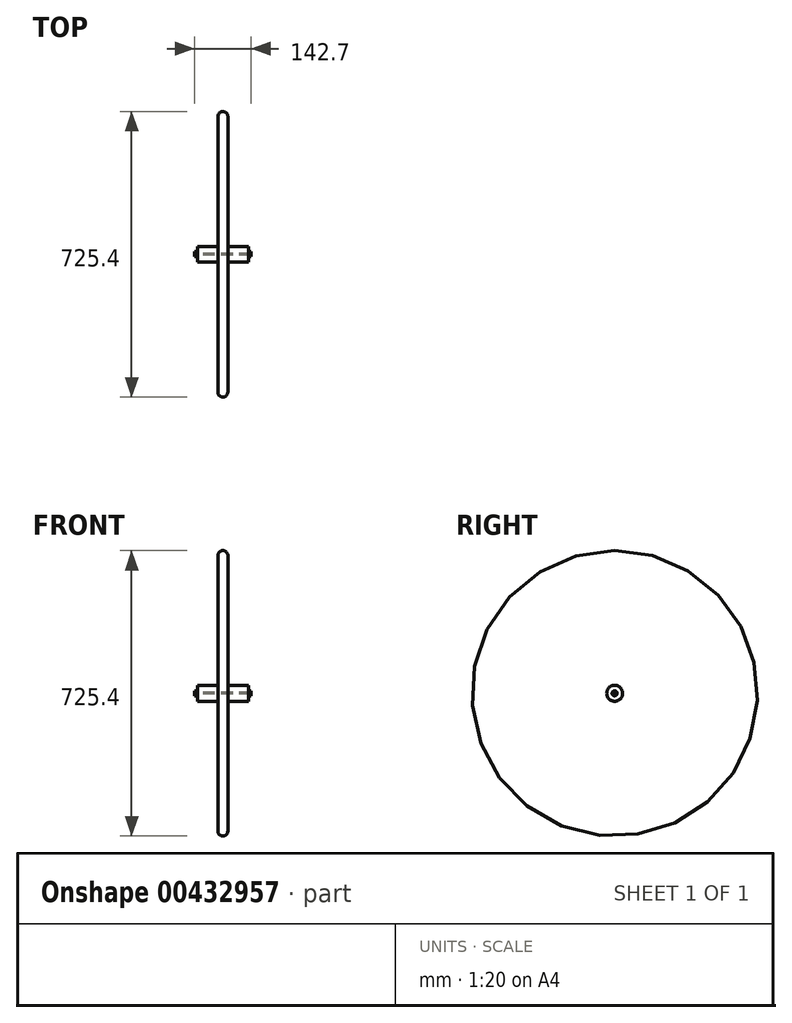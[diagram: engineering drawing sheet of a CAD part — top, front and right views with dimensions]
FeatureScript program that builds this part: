
annotation { "Feature Type Name" : "Feature", "Feature Type Description" : "" }
export const myFeature = defineFeature(function(context is Context, id is Id, definition is map)
    precondition{}
    {
        {
            var Q0;
            Q0=qCreatedBy(makeId("Top.planeOp"),FACE);
            var sketch = newSketch(context, id + "F0", { "sketchPlane" : qUnion([Q0])});
            skLineSegment(sketch, "E0", {"start": v(-65, 20.22) * mm, "end": v(-12.7, 20.22) * mm});
            skLineSegment(sketch, "E1", {"start": v(-75.47, 0) * mm, "end": v(74.77, 0) * mm});
            skLineSegment(sketch, "E2", {"start": v(65, 20.22) * mm, "end": v(65, 6.35) * mm});
            skLineSegment(sketch, "E3", {"start": v(65, 6.35) * mm, "end": v(65, 6.35) * mm});
            skLineSegment(sketch, "E4", {"start": v(71.35, 6.35) * mm, "end": v(65, 6.35) * mm});
            skLineSegment(sketch, "E5", {"start": v(-65, 20.22) * mm, "end": v(-65, 6.35) * mm});
            skLineSegment(sketch, "E6", {"start": v(-65, 6.35) * mm, "end": v(-71.35, 6.35) * mm});
            skLineSegment(sketch, "E7", {"start": v(-71.35, 6.35) * mm, "end": v(-71.35, 1.84) * mm});
            skLineSegment(sketch, "E8", {"start": v(71.35, 6.35) * mm, "end": v(71.35, 1.57) * mm});
            skLineSegment(sketch, "E9", {"start": v(-71.35, 1.84) * mm, "end": v(71.35, 1.57) * mm});
            skArc(sketch, "E10", {"start": v(12.7, 350) * mm, "mid": v(0, 362.7) * mm, "end": v(-12.7, 350) * mm});
            skLineSegment(sketch, "E11", {"start": v(12.7, 350) * mm, "end": v(12.7, 20.22) * mm});
            skLineSegment(sketch, "E12", {"start": v(-12.7, 350) * mm, "end": v(-12.7, 20.22) * mm});
            skLineSegment(sketch, "E13.trimOffspring", {"start": v(12.7, 20.22) * mm, "end": v(65, 20.22) * mm});
            skSolve(sketch);
        }
        {
            var Q0;
            Q0=makeQuery(id+"F0.imprint","IMPRINT",FACE,{"disambiguationData":[TD([[makeQuery(id+"F0.imprint","IMPRINT",EDGE,{"derivedFrom":sQuery(id+"F0.wireOp",EDGE,"E0")}),-1.0]])]});
            var Q1;
            Q1=sQuery(id+"F0.wireOp",EDGE,"E1");
            revolve(context, id + "F1", {"entities" : qUnion([Q0]), "axis" : qUnion([Q1]), "revolveType" : RevolveType.FULL});
        }
    });
